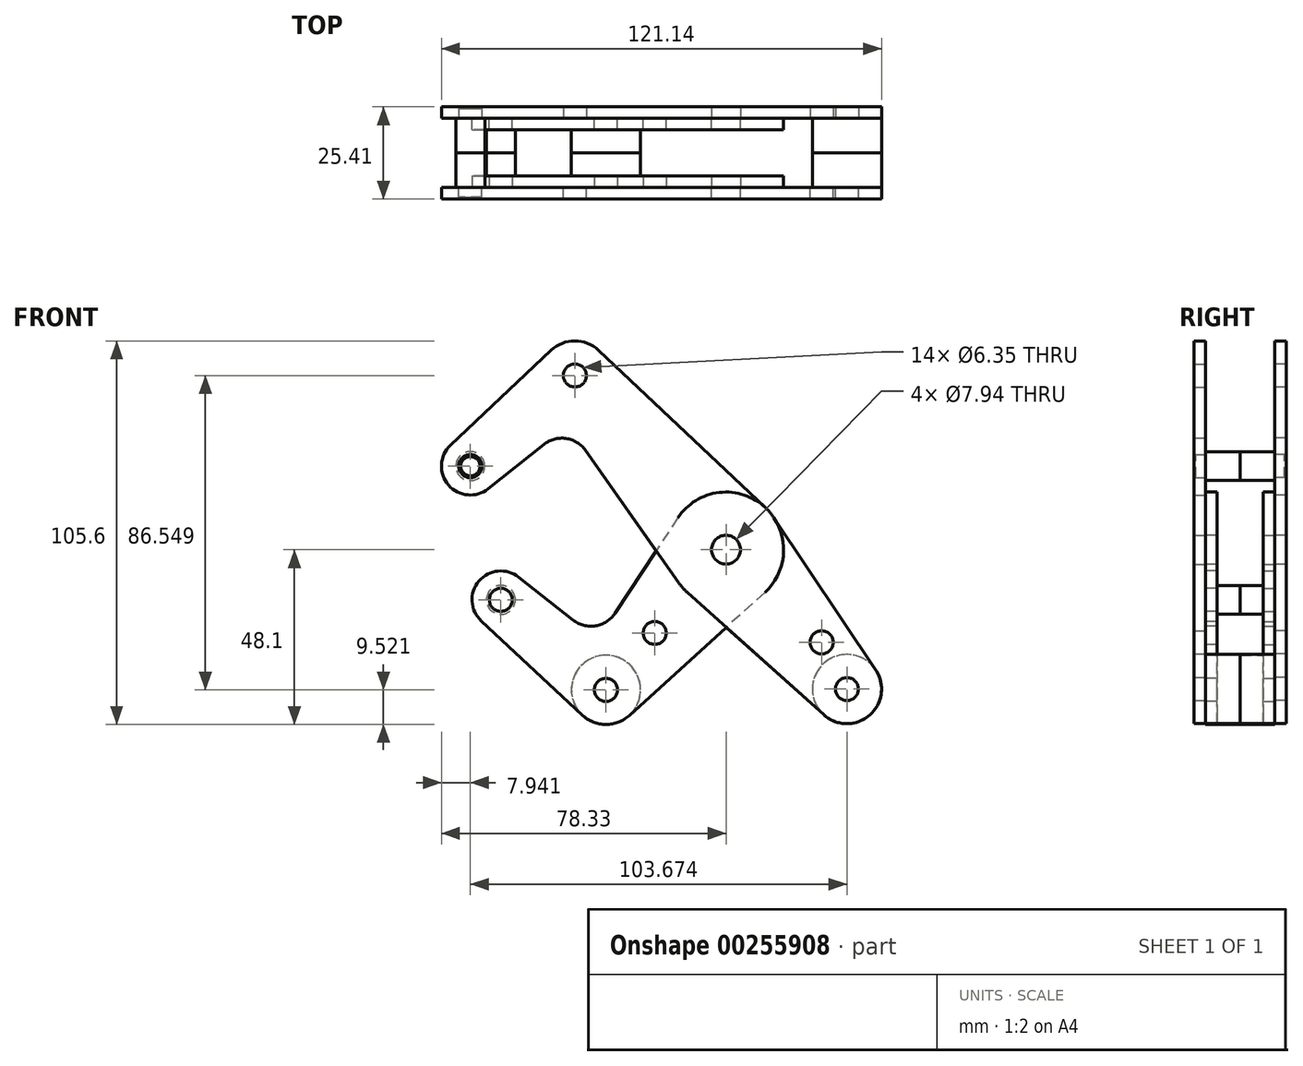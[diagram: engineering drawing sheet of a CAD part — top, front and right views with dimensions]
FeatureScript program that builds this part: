
annotation { "Feature Type Name" : "Feature", "Feature Type Description" : "" }
export const myFeature = defineFeature(function(context is Context, id is Id, definition is map)
    precondition{}
    {
        {
            var Q0;
            Q0=qCreatedBy(makeId("Front.planeOp"),FACE);
            var sketch = newSketch(context, id + "F0", { "sketchPlane" : qUnion([Q0])});
            skLineSegment(sketch, "E0", {"start": v(-41.6, 47.97) * mm, "end": v(41.6, -47.97) * mm, "construction": true});
            skCircle(sketch, "E1", {"center": v(0, 0) * mm, "radius": 3.18 * mm});
            skCircle(sketch, "E2", {"center": v(33.29, -38.38) * mm, "radius": 3.18 * mm});
            skCircle(sketch, "E3", {"center": v(-41.6, 47.97) * mm, "radius": 3.18 * mm});
            skCircle(sketch, "E4", {"center": v(-70.39, 23) * mm, "radius": 3.18 * mm});
            skLineSegment(sketch, "E5", {"start": v(-41.6, 47.97) * mm, "end": v(-70.39, 23) * mm, "construction": true});
            skCircle(sketch, "E6", {"center": v(33.29, -38.38) * mm, "radius": 9.53 * mm});
            skCircle(sketch, "E7", {"center": v(-70.39, 23) * mm, "radius": 7.94 * mm});
            skCircle(sketch, "E8", {"center": v(-41.6, 47.97) * mm, "radius": 9.53 * mm});
            skLineSegment(sketch, "E9", {"start": v(-75.83, 28.78) * mm, "end": v(-48.14, 54.9) * mm});
            skLineSegment(sketch, "E10", {"start": v(-65.44, 16.8) * mm, "end": v(-50.15, 28.98) * mm});
            skCircle(sketch, "E11", {"center": v(0, 0) * mm, "radius": 15.88 * mm});
            skLineSegment(sketch, "E12", {"start": v(-35.07, 54.9) * mm, "end": v(10.9, 11.55) * mm});
            skLineSegment(sketch, "E13", {"start": v(-38.72, 27.35) * mm, "end": v(-12.97, -9.15) * mm});
            skLineSegment(sketch, "E14", {"start": v(-10.6, -11.82) * mm, "end": v(26.93, -45.47) * mm});
            skLineSegment(sketch, "E15", {"start": v(13.2, 8.82) * mm, "end": v(41.2, -33.08) * mm});
            skArc(sketch, "E16.filletArc", {"start": v(-38.72, 27.35) * mm, "mid": v(-44.08, 30.63) * mm, "end": v(-50.15, 28.98) * mm});
            skLineSegment(sketch, "E17", {"start": v(0, 0) * mm, "end": v(-33.05, -38.58) * mm, "construction": true});
            skLineSegment(sketch, "E18", {"start": v(-33.05, -38.58) * mm, "end": v(-61.98, -13.8) * mm, "construction": true});
            skCircle(sketch, "E19", {"center": v(-61.98, -13.8) * mm, "radius": 3.18 * mm});
            skCircle(sketch, "E20", {"center": v(-33.05, -38.58) * mm, "radius": 3.18 * mm});
            skCircle(sketch, "E21", {"center": v(-61.98, -13.8) * mm, "radius": 7.94 * mm});
            skCircle(sketch, "E22", {"center": v(-33.05, -38.58) * mm, "radius": 9.53 * mm});
            skLineSegment(sketch, "E23", {"start": v(-57.08, -7.55) * mm, "end": v(-42.08, -19.35) * mm});
            skLineSegment(sketch, "E24", {"start": v(-67.4, -19.6) * mm, "end": v(-39.54, -45.55) * mm});
            skLineSegment(sketch, "E25", {"start": v(-13.25, 8.74) * mm, "end": v(-30.55, -17.48) * mm});
            skLineSegment(sketch, "E26", {"start": v(10.67, -11.75) * mm, "end": v(-26.65, -45.63) * mm});
            skArc(sketch, "E27.filletArc", {"start": v(-42.08, -19.35) * mm, "mid": v(-35.9, -20.95) * mm, "end": v(-30.55, -17.48) * mm});
            skCircle(sketch, "E28", {"center": v(-19.62, -22.9) * mm, "radius": 3.18 * mm});
            skCircle(sketch, "E29", {"center": v(26.32, -25.5) * mm, "radius": 3.18 * mm});
            skLineSegment(sketch, "E30", {"start": v(26.32, -25.5) * mm, "end": v(23.92, -27.58) * mm, "construction": true});
            skCircle(sketch, "E31", {"center": v(0, 0) * mm, "radius": 3.97 * mm});
            skSolve(sketch);
        }
        {
            var Q0;
            Q0=qCreatedBy(makeId("Front.planeOp"),FACE);
            cPlane(context, id + "F1", {"entities" : qUnion([Q0]), "cplaneType" : CPlaneType.OFFSET, "offset" : 9.52 * mm, "oppositeDirection" : true, "width" : 254 * mm, "height" : 254 * mm});
        }
        {
            var Q0;
            {var subQ1=sQuery(id+"F0.wireOp",EDGE,"E9");Q0=makeQuery(id+"F0.imprint","IMPRINT",FACE,{"disambiguationData":[TD([[makeQuery(id+"F0.imprint","IMPRINT",EDGE,{"derivedFrom":subQ1}),-1.0]])]});}
            var Q1;
            Q1=makeQuery(id+"F0.imprint","IMPRINT",FACE,{"disambiguationData":[TD([[makeQuery(id+"F0.imprint","IMPRINT",EDGE,{"derivedFrom":sQuery(id+"F0.wireOp",EDGE,"E4")}),-1.0]])]});
            var Q2;
            Q2=makeQuery(id+"F0.imprint","IMPRINT",FACE,{"disambiguationData":[TD([[makeQuery(id+"F0.imprint","IMPRINT",EDGE,{"derivedFrom":sQuery(id+"F0.wireOp",EDGE,"E3")}),-1.0]])]});
            var Q3;
            Q3=makeQuery(id+"F0.imprint","IMPRINT",FACE,{"disambiguationData":[TD([[makeQuery(id+"F0.imprint","IMPRINT",EDGE,{"derivedFrom":sQuery(id+"F0.wireOp",EDGE,"E31")}),-1.0]])]});
            var Q4;
            {var subQ0=sQuery(id+"F0.wireOp",EDGE,"E13");var subQ1=sQuery(id+"F0.wireOp",EDGE,"E11");var subQ2=makeQuery(id+"F0.imprint","INTERSECT",VERTEX,{"derivedFrom":[subQ1,subQ0]});Q4=makeQuery(id+"F0.imprint","IMPRINT",FACE,{"disambiguationData":[TD([[makeQuery(id+"F0.imprint","IMPRINT",EDGE,{"disambiguationData":[TD([[subQ2,1.0]])],"derivedFrom":subQ1}),-1.0]])]});}
            var Q5;
            {var subQ0=sQuery(id+"F0.wireOp",EDGE,"E14");var subQ1=sQuery(id+"F0.wireOp",EDGE,"E11");var subQ2=makeQuery(id+"F0.imprint","INTERSECT",VERTEX,{"derivedFrom":[subQ1,subQ0]});Q5=makeQuery(id+"F0.imprint","IMPRINT",FACE,{"disambiguationData":[TD([[makeQuery(id+"F0.imprint","IMPRINT",EDGE,{"disambiguationData":[TD([[subQ2,-1.0]])],"derivedFrom":subQ1}),-1.0]])]});}
            var Q6;
            {var subQ0=sQuery(id+"F0.wireOp",EDGE,"E15");Q6=makeQuery(id+"F0.imprint","IMPRINT",FACE,{"disambiguationData":[TD([[makeQuery(id+"F0.imprint","IMPRINT",EDGE,{"derivedFrom":subQ0}),-1.0]])]});}
            var Q7;
            Q7=makeQuery(id+"F0.imprint","IMPRINT",FACE,{"disambiguationData":[TD([[makeQuery(id+"F0.imprint","IMPRINT",EDGE,{"derivedFrom":sQuery(id+"F0.wireOp",EDGE,"E2")}),-1.0]])]});
            extrude(context, id + "F2", {"entities" : qUnion([Q0, Q1, Q2, Q3, Q4, Q5, Q6, Q7]), "depth" : 3.17 * mm});
        }
        {
            var Q0;
            Q0=makeQuery(id+"F0.imprint","IMPRINT",FACE,{"disambiguationData":[TD([[makeQuery(id+"F0.imprint","IMPRINT",EDGE,{"derivedFrom":sQuery(id+"F0.wireOp",EDGE,"E31")}),-1.0]])]});
            var Q1;
            {var subQ0=sQuery(id+"F0.wireOp",EDGE,"E14");var subQ1=sQuery(id+"F0.wireOp",EDGE,"E11");var subQ2=makeQuery(id+"F0.imprint","INTERSECT",VERTEX,{"derivedFrom":[subQ1,subQ0]});Q1=makeQuery(id+"F0.imprint","IMPRINT",FACE,{"disambiguationData":[TD([[makeQuery(id+"F0.imprint","IMPRINT",EDGE,{"disambiguationData":[TD([[subQ2,-1.0]])],"derivedFrom":subQ1}),-1.0]])]});}
            var Q2;
            {var subQ0=sQuery(id+"F0.wireOp",EDGE,"E13");var subQ1=sQuery(id+"F0.wireOp",EDGE,"E11");var subQ2=makeQuery(id+"F0.imprint","INTERSECT",VERTEX,{"derivedFrom":[subQ1,subQ0]});Q2=makeQuery(id+"F0.imprint","IMPRINT",FACE,{"disambiguationData":[TD([[makeQuery(id+"F0.imprint","IMPRINT",EDGE,{"disambiguationData":[TD([[subQ2,1.0]])],"derivedFrom":subQ1}),-1.0]])]});}
            var Q3;
            {var subQ10=sQuery(id+"F0.wireOp",EDGE,"E23");Q3=makeQuery(id+"F0.imprint","IMPRINT",FACE,{"disambiguationData":[TD([[makeQuery(id+"F0.imprint","IMPRINT",EDGE,{"derivedFrom":subQ10}),-1.0]])]});}
            var Q4;
            Q4=makeQuery(id+"F0.imprint","IMPRINT",FACE,{"disambiguationData":[TD([[makeQuery(id+"F0.imprint","IMPRINT",EDGE,{"derivedFrom":sQuery(id+"F0.wireOp",EDGE,"E20")}),-1.0]])]});
            var Q5;
            Q5=makeQuery(id+"F0.imprint","IMPRINT",FACE,{"disambiguationData":[TD([[makeQuery(id+"F0.imprint","IMPRINT",EDGE,{"derivedFrom":sQuery(id+"F0.wireOp",EDGE,"E19")}),-1.0]])]});
            extrude(context, id + "F3", {"entities" : qUnion([Q0, Q1, Q2, Q3, Q4, Q5]), "oppositeDirection" : true, "depth" : 3.17 * mm});
        }
        {
            var Q0;
            Q0=makeQuery(id+"F2.opExtrude","CAP_FACE",FACE,{"disambiguationData":[OSD([sQuery(id+"F0.wireOp",EDGE,"E2"),sQuery(id+"F0.wireOp",EDGE,"E3"),sQuery(id+"F0.wireOp",EDGE,"E4"),sQuery(id+"F0.wireOp",EDGE,"E6"),sQuery(id+"F0.wireOp",EDGE,"E7"),sQuery(id+"F0.wireOp",EDGE,"E8"),sQuery(id+"F0.wireOp",EDGE,"E9"),sQuery(id+"F0.wireOp",EDGE,"E10"),sQuery(id+"F0.wireOp",EDGE,"E11"),sQuery(id+"F0.wireOp",EDGE,"E12"),sQuery(id+"F0.wireOp",EDGE,"E13"),sQuery(id+"F0.wireOp",EDGE,"E14"),sQuery(id+"F0.wireOp",EDGE,"E15"),sQuery(id+"F0.wireOp",EDGE,"E16.filletArc"),sQuery(id+"F0.wireOp",EDGE,"E29"),sQuery(id+"F0.wireOp",EDGE,"E31")])],"isStart":false});
            var sketch = newSketch(context, id + "F4", { "sketchPlane" : qUnion([Q0])});
            skCircle(sketch, "E32", {"center": v(-70.39, 23) * mm, "radius": 3.98 * mm});
            skCircle(sketch, "E33", {"center": v(33.29, -38.38) * mm, "radius": 9.53 * mm});
            skSolve(sketch);
        }
        {
            var Q0;
            Q0=makeQuery(id+"F3.opExtrude","CAP_FACE",FACE,{"disambiguationData":[OSD([sQuery(id+"F0.wireOp",EDGE,"E11"),sQuery(id+"F0.wireOp",EDGE,"E19"),sQuery(id+"F0.wireOp",EDGE,"E20"),sQuery(id+"F0.wireOp",EDGE,"E21"),sQuery(id+"F0.wireOp",EDGE,"E22"),sQuery(id+"F0.wireOp",EDGE,"E23"),sQuery(id+"F0.wireOp",EDGE,"E24"),sQuery(id+"F0.wireOp",EDGE,"E25"),sQuery(id+"F0.wireOp",EDGE,"E26"),sQuery(id+"F0.wireOp",EDGE,"E27.filletArc"),sQuery(id+"F0.wireOp",EDGE,"E28"),sQuery(id+"F0.wireOp",EDGE,"E31")])],"isStart":true});
            var sketch = newSketch(context, id + "F5", { "sketchPlane" : qUnion([Q0])});
            skCircle(sketch, "E34", {"center": v(-33.05, -38.58) * mm, "radius": 9.53 * mm});
            skCircle(sketch, "E35", {"center": v(-61.98, -13.8) * mm, "radius": 3.98 * mm});
            skSolve(sketch);
        }
        {
            var Q0;
            Q0=qSketchRegion(id+"F4",true);
            var Q1;
            Q1=qSketchRegion(id+"F5",true);
            var Q2;
            Q2=sQuery(id+"F5.wireOp",EDGE,"E34");
            var Q3;
            Q3=sQuery(id+"F4.wireOp",EDGE,"E33");
            var Q4;
            Q4=sQuery(id+"F5.wireOp",EDGE,"E35");
            var Q5;
            Q5=sQuery(id+"F4.wireOp",EDGE,"E32");
            var Q6;
            Q6=qCreatedBy(id+"F1.planeOp",FACE);
            extrude(context, id + "F6", {"entities" : qUnion([Q0, Q1]), "surfaceEntities" : qUnion([Q2, Q3, Q4, Q5]), "endBound" : BoundingType.UP_TO_SURFACE, "oppositeDirection" : true, "endBoundEntityFace" : qUnion([Q6]), "depth" : 25.4 * mm});
        }
        {
            var Q0;
            Q0=makeQuery(id+"F2.opExtrude","SWEPT_BODY",BODY,{"disambiguationData":[OSD([sQuery(id+"F0.wireOp",EDGE,"E2"),sQuery(id+"F0.wireOp",EDGE,"E3"),sQuery(id+"F0.wireOp",EDGE,"E4"),sQuery(id+"F0.wireOp",EDGE,"E6"),sQuery(id+"F0.wireOp",EDGE,"E7"),sQuery(id+"F0.wireOp",EDGE,"E8"),sQuery(id+"F0.wireOp",EDGE,"E9"),sQuery(id+"F0.wireOp",EDGE,"E10"),sQuery(id+"F0.wireOp",EDGE,"E11"),sQuery(id+"F0.wireOp",EDGE,"E12"),sQuery(id+"F0.wireOp",EDGE,"E13"),sQuery(id+"F0.wireOp",EDGE,"E14"),sQuery(id+"F0.wireOp",EDGE,"E15"),sQuery(id+"F0.wireOp",EDGE,"E16.filletArc"),sQuery(id+"F0.wireOp",EDGE,"E29"),sQuery(id+"F0.wireOp",EDGE,"E31")])]});
            var Q1;
            Q1=makeQuery(id+"F3.opExtrude","SWEPT_BODY",BODY,{"disambiguationData":[OSD([sQuery(id+"F0.wireOp",EDGE,"E11"),sQuery(id+"F0.wireOp",EDGE,"E19"),sQuery(id+"F0.wireOp",EDGE,"E20"),sQuery(id+"F0.wireOp",EDGE,"E21"),sQuery(id+"F0.wireOp",EDGE,"E22"),sQuery(id+"F0.wireOp",EDGE,"E23"),sQuery(id+"F0.wireOp",EDGE,"E24"),sQuery(id+"F0.wireOp",EDGE,"E25"),sQuery(id+"F0.wireOp",EDGE,"E26"),sQuery(id+"F0.wireOp",EDGE,"E27.filletArc"),sQuery(id+"F0.wireOp",EDGE,"E28"),sQuery(id+"F0.wireOp",EDGE,"E31")])]});
            var Q2;
            Q2=makeQuery(id+"F6.opExtrude","SWEPT_BODY",BODY,{"disambiguationData":[OSD([sQuery(id+"F4.wireOp",EDGE,"E32")])]});
            var Q3;
            Q3=makeQuery(id+"F6.opExtrude","SWEPT_BODY",BODY,{"disambiguationData":[OSD([sQuery(id+"F5.wireOp",EDGE,"E35")])]});
            var Q4;
            Q4=makeQuery(id+"F6.opExtrude","SWEPT_BODY",BODY,{"disambiguationData":[OSD([sQuery(id+"F5.wireOp",EDGE,"E34")])]});
            var Q5;
            Q5=makeQuery(id+"F6.opExtrude","SWEPT_BODY",BODY,{"disambiguationData":[OSD([sQuery(id+"F4.wireOp",EDGE,"E33")])]});
            booleanBodies(context, id + "F7", {"operationType" : BooleanOperationType.SUBTRACTION, "tools" : qUnion([Q0, Q1]), "targets" : qUnion([Q2, Q3, Q4, Q5]), "keepTools" : true});
        }
        {
            var Q0;
            Q0=makeQuery(id+"F7.opBoolean","COPY",EDGE,{"derivedFrom":makeQuery(id+"F2.opExtrude","CAP_EDGE",EDGE,{"disambiguationData":[OSD([sQuery(id+"F0.wireOp",EDGE,"E2")])],"isStart":false})});
            var Q1;
            Q1=makeQuery(id+"F7.opBoolean","COPY",EDGE,{"derivedFrom":makeQuery(id+"F3.opExtrude","CAP_EDGE",EDGE,{"disambiguationData":[OSD([sQuery(id+"F0.wireOp",EDGE,"E20")])],"isStart":true})});
            var Q2;
            Q2=makeQuery(id+"F7.opBoolean","COPY",EDGE,{"derivedFrom":makeQuery(id+"F3.opExtrude","CAP_EDGE",EDGE,{"disambiguationData":[OSD([sQuery(id+"F0.wireOp",EDGE,"E19")])],"isStart":true})});
            var Q3;
            Q3=makeQuery(id+"F6.opExtrude","CAP_FACE",FACE,{"disambiguationData":[OSD([sQuery(id+"F4.wireOp",EDGE,"E32")])],"isStart":true});
            chamfer(context, id + "F8", {"entities" : qUnion([Q0, Q1, Q2, Q3]), "width" : 0.5 * mm, "tangentPropagation" : true});
        }
        {
            var Q0;
            Q0=makeQuery(id+"F6.opExtrude","SWEPT_BODY",BODY,{"disambiguationData":[OSD([sQuery(id+"F5.wireOp",EDGE,"E35")])]});
            var Q1;
            Q1=makeQuery(id+"F6.opExtrude","SWEPT_BODY",BODY,{"disambiguationData":[OSD([sQuery(id+"F5.wireOp",EDGE,"E34")])]});
            var Q2;
            Q2=makeQuery(id+"F6.opExtrude","SWEPT_BODY",BODY,{"disambiguationData":[OSD([sQuery(id+"F4.wireOp",EDGE,"E33")])]});
            var Q3;
            Q3=makeQuery(id+"F6.opExtrude","SWEPT_BODY",BODY,{"disambiguationData":[OSD([sQuery(id+"F4.wireOp",EDGE,"E32")])]});
            var Q4;
            Q4=qCreatedBy(id+"F1.planeOp",FACE);
            mirror(context, id + "F9", {"entities" : qUnion([Q0, Q1, Q2, Q3]), "mirrorPlane" : qUnion([Q4])});
        }
        {
            var Q0;
            Q0=makeQuery(id+"F2.opExtrude","SWEPT_BODY",BODY,{"disambiguationData":[OSD([sQuery(id+"F0.wireOp",EDGE,"E2"),sQuery(id+"F0.wireOp",EDGE,"E3"),sQuery(id+"F0.wireOp",EDGE,"E4"),sQuery(id+"F0.wireOp",EDGE,"E6"),sQuery(id+"F0.wireOp",EDGE,"E7"),sQuery(id+"F0.wireOp",EDGE,"E8"),sQuery(id+"F0.wireOp",EDGE,"E9"),sQuery(id+"F0.wireOp",EDGE,"E10"),sQuery(id+"F0.wireOp",EDGE,"E11"),sQuery(id+"F0.wireOp",EDGE,"E12"),sQuery(id+"F0.wireOp",EDGE,"E13"),sQuery(id+"F0.wireOp",EDGE,"E14"),sQuery(id+"F0.wireOp",EDGE,"E15"),sQuery(id+"F0.wireOp",EDGE,"E16.filletArc"),sQuery(id+"F0.wireOp",EDGE,"E29"),sQuery(id+"F0.wireOp",EDGE,"E31")])]});
            var Q1;
            Q1=makeQuery(id+"F3.opExtrude","SWEPT_BODY",BODY,{"disambiguationData":[OSD([sQuery(id+"F0.wireOp",EDGE,"E11"),sQuery(id+"F0.wireOp",EDGE,"E19"),sQuery(id+"F0.wireOp",EDGE,"E20"),sQuery(id+"F0.wireOp",EDGE,"E21"),sQuery(id+"F0.wireOp",EDGE,"E22"),sQuery(id+"F0.wireOp",EDGE,"E23"),sQuery(id+"F0.wireOp",EDGE,"E24"),sQuery(id+"F0.wireOp",EDGE,"E25"),sQuery(id+"F0.wireOp",EDGE,"E26"),sQuery(id+"F0.wireOp",EDGE,"E27.filletArc"),sQuery(id+"F0.wireOp",EDGE,"E28"),sQuery(id+"F0.wireOp",EDGE,"E31")])]});
            var Q2;
            Q2=qCreatedBy(id+"F1.planeOp",FACE);
            mirror(context, id + "F10", {"entities" : qUnion([Q0, Q1]), "mirrorPlane" : qUnion([Q2])});
        }
    });
